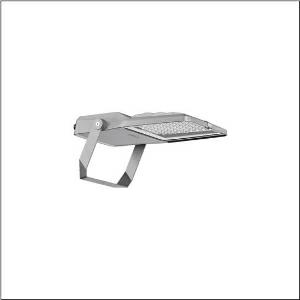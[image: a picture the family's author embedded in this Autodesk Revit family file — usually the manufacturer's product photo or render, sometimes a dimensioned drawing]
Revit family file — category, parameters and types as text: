
# Revit family: floodlight_fl_21_mini___rs12_5xa7772b5b1a_aea4
name_source: partatom
category: Lighting Fixtures
units: mm (PartAtom-declared; Revit-internal decimal feet)

## family parameters
Cut with Voids When Loaded = No
Host = Face
Light Source = No
Part Type = Normal
Room Calculation Point = No
Round Connector Dimension = Use Diameter
Shared = No

## types (1)
- --- (1 x LED, 5880 lm, 45.5 W, 4000K)
    Apparent Load = 46 VA
    CIE Flux Codes = 79 92 99 100 100
    Color Rendering = 80
    Color Temperature = 4000K
    Default Elevation = 1800 mm
    Description = Floodlight FL 21 mini, floodlight, primary light control with lens, of PMMA, primary optical cover: protective disc, of toughened safety glass, transparent, light distribution: RS12, light emission: direct distribution, installation type: surface-mounted, LED, High Power LED, rated luminous flux: 5.880lm, luminous efficacy: 129lm/W, light colour: 840, colour temperature: 4000K, control gear: ECG iQ, control: Street-Remote, Auto-Match, Temp-Guard, Night-Set, Smart-Wire, Desk-Remote (wireless, voltage-free reading and setting of iQ features in the workshop via application-optimized NFC function/RFID function), optimised constant luminous flux control (CLO 2.0), with terminal, 6-pole, mains connection: 220..240V, AC, 50/60Hz, start of lifetime: 46W, end of lifetime: 48W, reduction: 22W, luminaire housing, of diecast aluminium, powder-coated, Siteco® metallic grey (DB 702S), corrosivity category C5 according to DIN EN ISO 12944, mounting bracket, of steel, galvanised, powder-coated, Siteco® metallic grey (DB 702S), protection rating (complete): IP66, insulation class (complete): insulation class II (safety insulation), certification: CE, ENEC, VDE, protection symbol: D, impact resistance: IK08, permissible operating ambient temperature: -40..+40°C, permissible operating ambient temperature for outdoor applications: -40..+50°C, standard: DIN EN 12944, packaging unit: 1 piece

Light Distribution: RS12
    Height = 70 mm
    Lamp = 1 x LED
    Lamp Light Flux = 5880 lm
    Lamp Power = 45.5 W
    Lamp count = 1
    Length = 485 mm
    Luminous efficacy = 129 lm/W
    Manufacturer = Siteco
    ModVariant = No
    Model = 5XA7772B5B1A
    Number of Poles = 1
    OnlyDefault = Yes
    Power Factor = 1
    Product Name = Floodlight FL 21 mini | RS12
    Product group = floodlight | pylon top
    ProductGroupID = 6101
    Protection Class = Protection class II
    Protection Degree = IP 66
    RLX_Detail_Level = 1
    RlxData = <blob elided: 90617 chars, md5=4a9c3fae>
    Socket = socket
    Standby Power = 0 W
    System Light Flux = 5880 lm
    System Power = 46 W
    Type Comments = factory setting: luminous flux: 100 % | dim-lin: 254 | 463 mA
    Type Image = l_1006845.jpg
    URL = http://relux.com
    VarID = @adj_078847
    Voltage = 0 V
    Weight = 0.00 kg
    Width = 337 mm

## geometry (parser evidence)
native form markers: Blend x4, Sweep x13
no freeform markers — native parametric forms only
